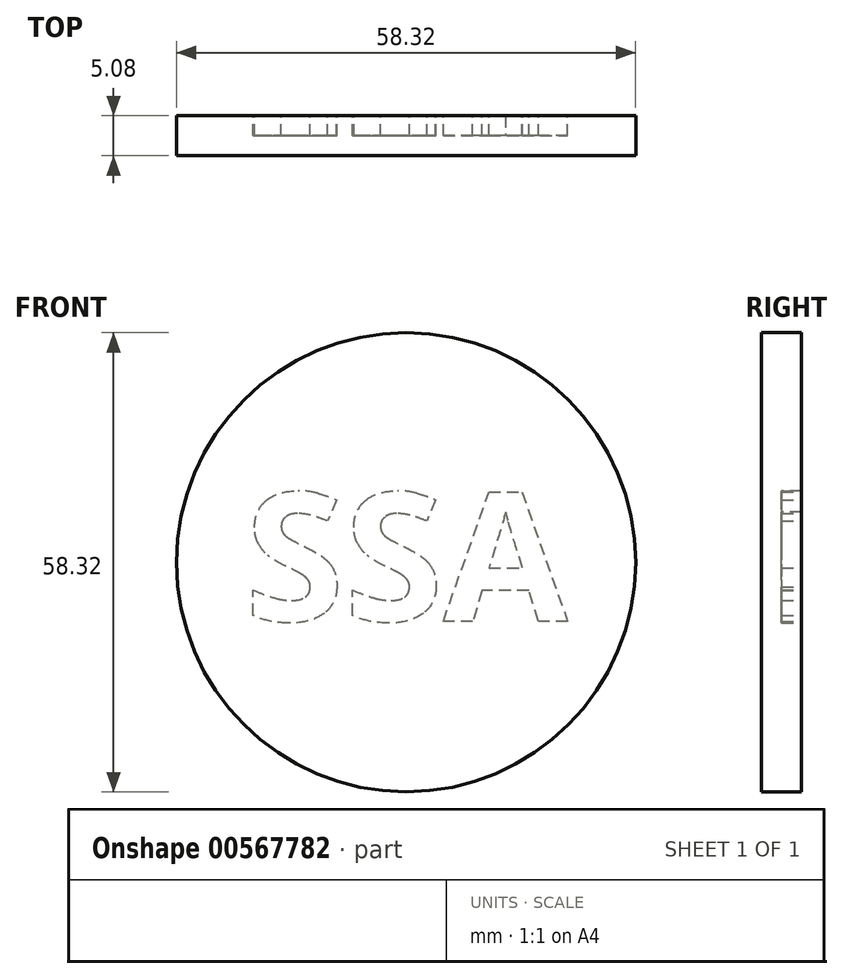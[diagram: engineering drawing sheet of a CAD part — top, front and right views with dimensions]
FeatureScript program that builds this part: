
annotation { "Feature Type Name" : "Feature", "Feature Type Description" : "" }
export const myFeature = defineFeature(function(context is Context, id is Id, definition is map)
    precondition{}
    {
        {
            var Q0;
            Q0=qCreatedBy(makeId("Front.planeOp"),FACE);
            var sketch = newSketch(context, id + "F0", { "sketchPlane" : qUnion([Q0])});
            skCircle(sketch, "E0", {"center": v(-26.37, -14.55) * mm, "radius": 29.16 * mm});
            skSolve(sketch);
        }
        {
            var Q0;
            Q0 = qSketchRegion(id + "F0", true);
            extrude(context, id + "F1", {"entities" : qUnion([Q0]), "depth" : 5.08 * mm, "offsetDistance" : 25.4 * mm});
        }
        {
            var Q0;
            Q0=qCreatedBy(makeId("Front.planeOp"),FACE);
            var sketch = newSketch(context, id + "F2", { "sketchPlane" : qUnion([Q0])});
            skText(sketch, "E1", { "text": "SSA", "fontName": "OpenSans-Bold.ttf"});
            const initialGuessF2  = {"E1": [-0.04686, -0.02204, 1, 0, 0.01648]};
            skSetInitialGuess(sketch, initialGuessF2);
            skSolve(sketch);
        }
        {
            var Q0;
            Q0 = qSketchRegion(id + "F2", true);
            extrude(context, id + "F3", {"entities" : qUnion([Q0]), "operationType" : NewBodyOperationType.REMOVE, "depth" : 2.54 * mm, "offsetDistance" : 25.4 * mm});
        }
    });
